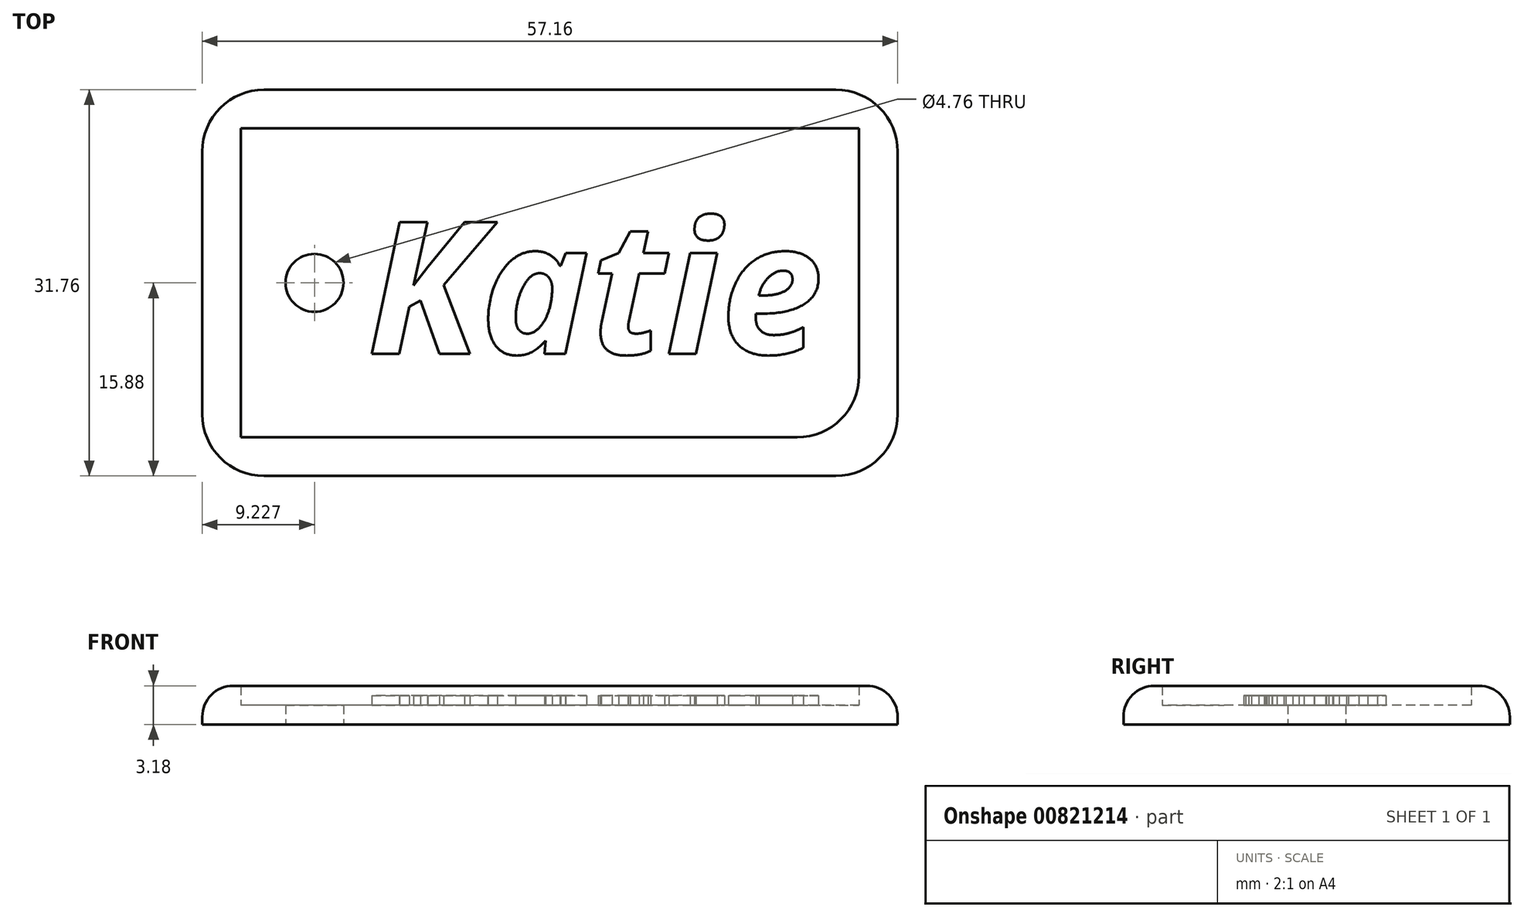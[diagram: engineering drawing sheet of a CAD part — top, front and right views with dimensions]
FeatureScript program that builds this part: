
annotation { "Feature Type Name" : "Feature", "Feature Type Description" : "" }
export const myFeature = defineFeature(function(context is Context, id is Id, definition is map)
    precondition{}
    {
        {
            var Q0;
            Q0=qCreatedBy(makeId("Top.planeOp"),FACE);
            var sketch = newSketch(context, id + "F0", { "sketchPlane" : qUnion([Q0])});
            skLineSegment(sketch, "E0.bottom", {"start": v(0, 0) * mm, "end": v(50.8, 0) * mm});
            skLineSegment(sketch, "E0.top", {"start": v(0, 25.4) * mm, "end": v(50.8, 25.4) * mm});
            skLineSegment(sketch, "E0.left", {"start": v(0, 0) * mm, "end": v(0, 25.4) * mm});
            skLineSegment(sketch, "E0.right", {"start": v(50.8, 0) * mm, "end": v(50.8, 25.4) * mm});
            skCircle(sketch, "E1", {"center": v(6.05, 12.7) * mm, "radius": 2.38 * mm});
            skPoint(sketch, "E1.centerSnap0", {"position": v(0, 12.7) * mm});
            skLineSegment(sketch, "E2.0", {"start": v(-3.18, 28.58) * mm, "end": v(53.98, 28.58) * mm});
            skLineSegment(sketch, "E2.1", {"start": v(-3.18, -3.18) * mm, "end": v(-3.18, 28.58) * mm});
            skLineSegment(sketch, "E2.2", {"start": v(-3.18, -3.18) * mm, "end": v(53.98, -3.18) * mm});
            skLineSegment(sketch, "E2.3", {"start": v(53.98, -3.18) * mm, "end": v(53.98, 28.57) * mm});
            skSolve(sketch);
        }
        {
            var Q0;
            Q0 = qSketchRegion(id + "F0", true);
            var Q1;
            Q1=makeQuery(id+"F0.imprint","IMPRINT",FACE,{"disambiguationData":[TD([[makeQuery(id+"F0.imprint","IMPRINT",EDGE,{"derivedFrom":sQuery(id+"F0.wireOp",EDGE,"E0.bottom")}),1.0]])]});
            extrude(context, id + "F1", {"entities" : qUnion([Q0, Q1]), "depth" : 1.59 * mm, "offsetDistance" : 25.4 * mm});
        }
        {
            var Q0;
            Q0 = qSketchRegion(id + "F0", true);
            extrude(context, id + "F2", {"entities" : qUnion([Q0]), "operationType" : NewBodyOperationType.ADD, "depth" : 3.17 * mm, "offsetDistance" : 25.4 * mm});
        }
        {
            var Q0;
            {var subQ0=sQuery(id+"F0.wireOp",EDGE,"E2.3");var subQ1=sQuery(id+"F0.wireOp",EDGE,"E2.2");Q0=makeQuery(id+"F2.boolean.opBoolean","MERGE",EDGE,{"derivedFrom":[makeQuery(id+"F1.opExtrude","SWEPT_EDGE",EDGE,{"disambiguationData":[OSD([subQ1,subQ0])]}),makeQuery(id+"F2.opExtrude","SWEPT_EDGE",EDGE,{"disambiguationData":[OSD([subQ1,subQ0])]})]});}
            var Q1;
            {var subQ0=sQuery(id+"F0.wireOp",EDGE,"E2.2");var subQ1=sQuery(id+"F0.wireOp",EDGE,"E2.1");Q1=makeQuery(id+"F2.boolean.opBoolean","MERGE",EDGE,{"derivedFrom":[makeQuery(id+"F1.opExtrude","SWEPT_EDGE",EDGE,{"disambiguationData":[OSD([subQ1,subQ0])]}),makeQuery(id+"F2.opExtrude","SWEPT_EDGE",EDGE,{"disambiguationData":[OSD([subQ1,subQ0])]})]});}
            var Q2;
            Q2=makeQuery(id+"F2.opExtrude","SWEPT_EDGE",EDGE,{"disambiguationData":[OSD([sQuery(id+"F0.wireOp",EDGE,"E0.bottom"),sQuery(id+"F0.wireOp",EDGE,"E0.right")])]});
            var Q3;
            {var subQ0=sQuery(id+"F0.wireOp",EDGE,"E2.3");var subQ1=sQuery(id+"F0.wireOp",EDGE,"E2.0");Q3=makeQuery(id+"F2.boolean.opBoolean","MERGE",EDGE,{"derivedFrom":[makeQuery(id+"F1.opExtrude","SWEPT_EDGE",EDGE,{"disambiguationData":[OSD([subQ1,subQ0])]}),makeQuery(id+"F2.opExtrude","SWEPT_EDGE",EDGE,{"disambiguationData":[OSD([subQ1,subQ0])]})]});}
            var Q4;
            {var subQ0=sQuery(id+"F0.wireOp",EDGE,"E2.1");var subQ1=sQuery(id+"F0.wireOp",EDGE,"E2.0");Q4=makeQuery(id+"F2.boolean.opBoolean","MERGE",EDGE,{"derivedFrom":[makeQuery(id+"F1.opExtrude","SWEPT_EDGE",EDGE,{"disambiguationData":[OSD([subQ1,subQ0])]}),makeQuery(id+"F2.opExtrude","SWEPT_EDGE",EDGE,{"disambiguationData":[OSD([subQ1,subQ0])]})]});}
            fillet(context, id + "F3", {"entities" : qUnion([Q0, Q1, Q2, Q3, Q4]), "radius" : 5.08 * mm, "tangentPropagation" : true, "allowEdgeOverflow" : false});
        }
        {
            var Q0;
            Q0=makeQuery(id+"F2.opExtrude","CAP_EDGE",EDGE,{"disambiguationData":[OSD([sQuery(id+"F0.wireOp",EDGE,"E2.2")])],"isStart":false});
            fillet(context, id + "F4", {"entities" : qUnion([Q0]), "radius" : 2.54 * mm, "tangentPropagation" : true, "allowEdgeOverflow" : false});
        }
        {
            var Q0;
            Q0=makeQuery(id+"F1.opExtrude","CAP_FACE",FACE,{"disambiguationData":[OSD([sQuery(id+"F0.wireOp",EDGE,"E1"),sQuery(id+"F0.wireOp",EDGE,"E2.0"),sQuery(id+"F0.wireOp",EDGE,"E2.1"),sQuery(id+"F0.wireOp",EDGE,"E2.2"),sQuery(id+"F0.wireOp",EDGE,"E2.3")])],"isStart":false});
            var sketch = newSketch(context, id + "F5", { "sketchPlane" : qUnion([Q0])});
            skText(sketch, "E3", { "text": "Katie", "fontName": "OpenSans-BoldItalic.ttf"});
            const initialGuessF5  = {"E3": [0.01037, 0.00687, 1, 0, 0.01092]};
            skSetInitialGuess(sketch, initialGuessF5);
            skSolve(sketch);
        }
        {
            var Q0;
            Q0 = qSketchRegion(id + "F5", true);
            extrude(context, id + "F6", {"entities" : qUnion([Q0]), "operationType" : NewBodyOperationType.ADD, "depth" : 0.8 * mm, "offsetDistance" : 25.4 * mm});
        }
    });
